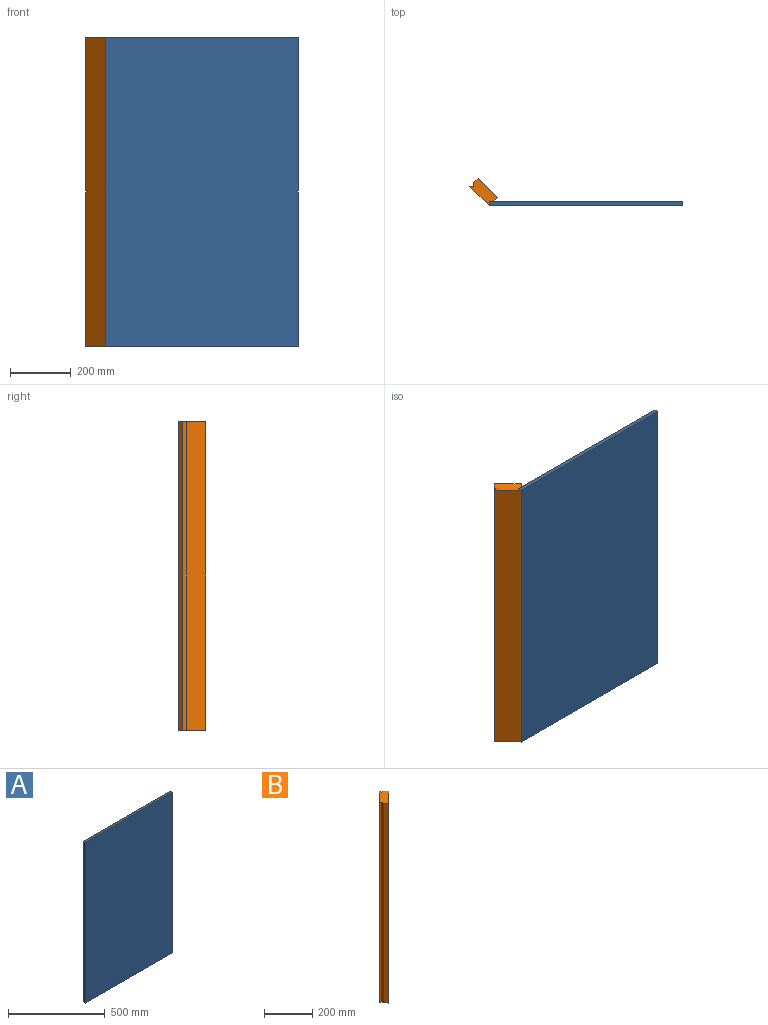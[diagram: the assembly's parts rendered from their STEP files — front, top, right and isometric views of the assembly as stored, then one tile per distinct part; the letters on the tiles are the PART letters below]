
ASSEMBLY  parts=2 mates=1
PART A: 6 faces, bbox 636.3x12.7x1016 mm
  f0: plane 1016x636.28mm, normal (0,-1,0), area 646456.8mm2, adj f1,f3,f4,f5
  f1: plane 1016x12.7mm, normal (1,0,0), area 12903.2mm2, adj f0,f2,f4,f5
  f2: plane 1016x636.28mm, normal (0,1,0), area 646456.8mm2, adj f1,f3,f4,f5
  f3: plane 1016x12.7mm, normal (-1,0,0), area 12903.2mm2, adj f0,f2,f4,f5
  f4: plane 636.28x12.7mm, normal (0,0,1), area 8080.7mm2, adj f0,f1,f2,f3
  f5: plane 636.28x12.7mm, normal (0,0,-1), area 8080.7mm2, adj f0,f1,f2,f3
PART B: 10 faces, bbox 89.8x89.8x1016 mm
  f0: plane 1016x14.24mm, normal (-0.71,-0.71,0), area 20461.7mm2, adj f1,f7,f8,f9
  f1: plane 1016x62.86mm, normal (0.71,-0.71,0), area 90322.4mm2, adj f0,f2,f8,f9
  f2: plane 1016x14.24mm, normal (0.71,0.71,0), area 20461.7mm2, adj f1,f3,f8,f9
  f3: plane 1016x12.7mm, normal (0,1,0), area 12903.2mm2, adj f2,f4,f8,f9
  f4: plane 1016x12.7mm, normal (1,0,0), area 12903.2mm2, adj f3,f5,f8,f9
  f5: plane 1016x62.86mm, normal (-0.71,0.71,0), area 90322.4mm2, adj f4,f6,f8,f9
  f6: plane 1016x12.7mm, normal (0,-1,0), area 12903.2mm2, adj f5,f7,f8,f9
  f7: plane 1016x12.7mm, normal (-1,0,0), area 12903.2mm2, adj f0,f6,f8,f9
  f8: plane 89.8x89.8mm, normal (0,0,1), area 3225.8mm2, adj f0,f1,f2,f3,f4,f5,f6,f7
  f9: plane 89.8x89.8mm, normal (0,0,-1), area 3225.8mm2, adj f0,f1,f2,f3,f4,f5,f6,f7
PLACE A at identity fixed
PLACE B rot(axis=(0,0,1),90deg) t=(0,50.16,0)mm
MATE fastened A.f4 <-> B.f8  axis (0,0,-1) through (31.43,31.43,1016)mm
